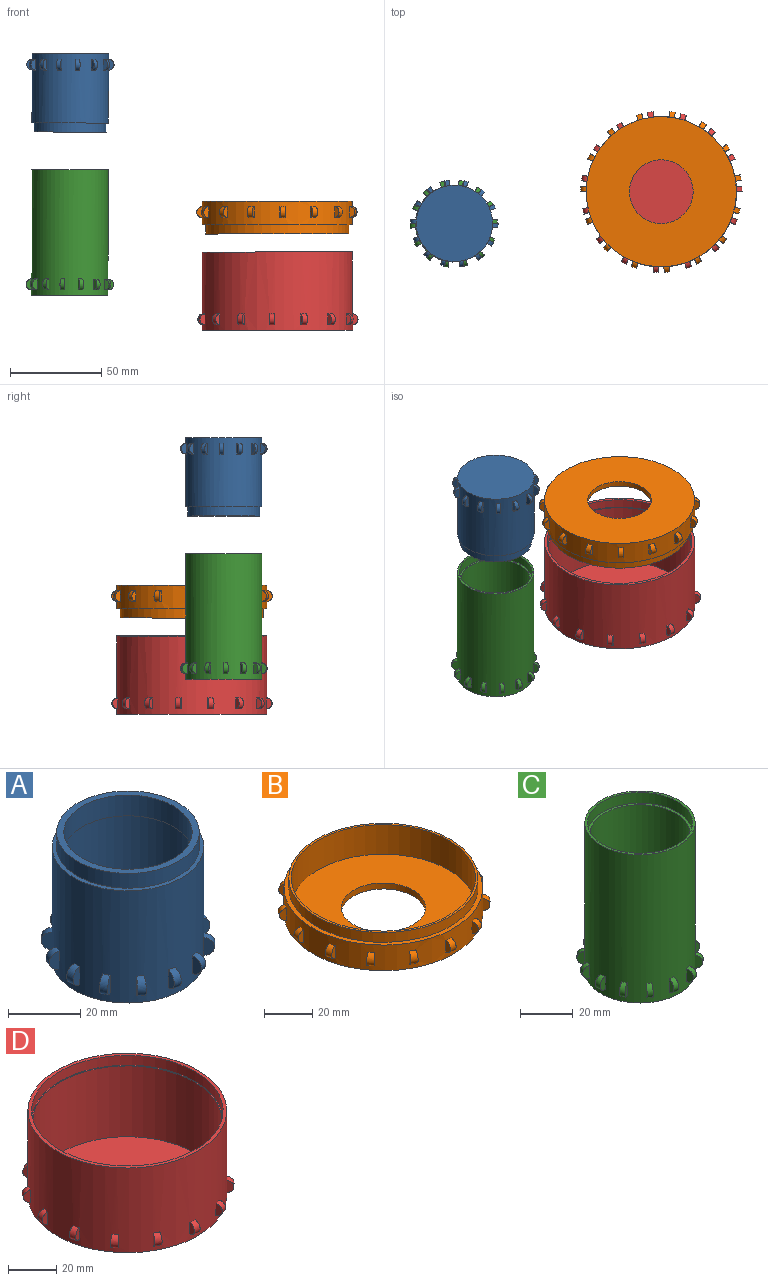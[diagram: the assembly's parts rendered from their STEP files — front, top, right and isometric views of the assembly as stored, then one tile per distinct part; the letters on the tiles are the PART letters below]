
ASSEMBLY  parts=4 mates=2
PART A: 51 faces, bbox 48.1x47.7x43 mm
  f0: torus R=21.01mm, axis (0,0,-1), area 21.6mm2, adj f22,f48,f49
  f1: torus R=21.01mm, axis (0,0,-1), area 21.6mm2, adj f22,f46,f47
  f2: torus R=21.01mm, axis (0,0,-1), area 21.6mm2, adj f22,f44,f45
  f3: torus R=21.01mm, axis (0,0,-1), area 21.6mm2, adj f22,f42,f43
  f4: torus R=21.01mm, axis (0,0,-1), area 21.6mm2, adj f22,f40,f41
  f5: torus R=21.01mm, axis (0,0,-1), area 21.6mm2, adj f22,f38,f39
  f6: torus R=21.01mm, axis (0,0,-1), area 21.6mm2, adj f22,f36,f37
  f7: torus R=21.01mm, axis (0,0,-1), area 21.6mm2, adj f22,f34,f35
  f8: torus R=21.01mm, axis (0,0,-1), area 21.6mm2, adj f22,f32,f33
  f9: torus R=21.01mm, axis (0,0,-1), area 21.6mm2, adj f22,f30,f31
  f10: torus R=21.01mm, axis (0,0,-1), area 21.6mm2, adj f22,f28,f29
  f11: torus R=21.01mm, axis (0,0,-1), area 21.6mm2, adj f22,f26,f27
  f12: torus R=21.01mm, axis (0,0,-1), area 21.6mm2, adj f22,f24,f25
  f13: torus R=21.01mm, axis (0,0,-1), area 21.6mm2, adj f22,f23,f50
  f14: cylinder r=19.75mm len=39.5mm, axis (0,0,-1), area 620.5mm2, adj f15,f16
  f15: plane 39.5x39.5mm, normal (0,0,1), area 235.6mm2, adj f14,f17
  f16: plane 42x42mm, normal (0,0,1), area 160mm2, adj f14,f22
  f17: cylinder r=17.75mm len=35.5mm, axis (0,0,-1), area 780.7mm2, adj f15,f19
  f18: cylinder r=19mm len=38mm, axis (0,0,-1), area 4058.9mm2, adj f19,f20
  f19: plane 38x38mm, normal (0,0,-1), area 144.3mm2, adj f17,f18
  f20: plane 38x38mm, normal (0,0,1), area 1134.1mm2, adj f18
  f21: plane 42x42mm, normal (0,0,-1), area 1385.4mm2, adj f22
  f22: cylinder r=21mm len=42mm, axis (0,0,-1), area 4838.1mm2, adj f0,f1,f2,f3,f4,f5,f6,f7
  f23: plane 6x2.83mm, normal (0.34,0.94,0), area 14.2mm2, adj f13,f22
  f24: plane 6x3.01mm, normal (0,-1,0), area 14.2mm2, adj f12,f22
  f25: plane 6x3mm, normal (-0.1,1,0), area 14.2mm2, adj f12,f22
  f26: plane 6x2.71mm, normal (0.43,-0.9,0), area 14.2mm2, adj f11,f22
  f27: plane 6x2.57mm, normal (-0.52,0.85,0), area 14.2mm2, adj f11,f22
  f28: plane 6x2.36mm, normal (0.78,-0.62,0), area 14.2mm2, adj f10,f22
  f29: plane 6x2.53mm, normal (-0.84,0.54,0), area 14.2mm2, adj f10,f22
  f30: plane 6x2.94mm, normal (0.97,-0.22,0), area 14.2mm2, adj f9,f22
  f31: plane 6x2.99mm, normal (-0.99,0.12,0), area 14.2mm2, adj f9,f22
  f32: plane 6x2.94mm, normal (0.97,0.22,0), area 14.2mm2, adj f8,f22
  f33: plane 6x2.86mm, normal (-0.95,-0.32,0), area 14.2mm2, adj f8,f22
  f34: plane 6x2.36mm, normal (0.78,0.62,0), area 14.2mm2, adj f7,f22
  f35: plane 6x2.16mm, normal (-0.72,-0.7,0), area 14.2mm2, adj f7,f22
  f36: plane 6x2.71mm, normal (0.43,0.9,0), area 14.2mm2, adj f6,f22
  f37: plane 6x2.83mm, normal (-0.34,-0.94,0), area 14.2mm2, adj f6,f22
  f38: plane 6x3.01mm, normal (0,1,0), area 14.2mm2, adj f5,f22
  f39: plane 6x3mm, normal (0.1,-1,0), area 14.2mm2, adj f5,f22
  f40: plane 6x2.71mm, normal (-0.43,0.9,0), area 14.2mm2, adj f4,f22
  f41: plane 6x2.57mm, normal (0.52,-0.85,0), area 14.2mm2, adj f4,f22
  f42: plane 6x2.36mm, normal (-0.78,0.62,0), area 14.2mm2, adj f3,f22
  f43: plane 6x2.53mm, normal (0.84,-0.54,0), area 14.2mm2, adj f3,f22
  f44: plane 6x2.94mm, normal (-0.97,0.22,0), area 14.2mm2, adj f2,f22
  f45: plane 6x2.99mm, normal (0.99,-0.12,0), area 14.2mm2, adj f2,f22
  f46: plane 6x2.94mm, normal (-0.97,-0.22,0), area 14.2mm2, adj f1,f22
  f47: plane 6x2.86mm, normal (0.95,0.32,0), area 14.2mm2, adj f1,f22
  f48: plane 6x2.36mm, normal (-0.78,-0.62,0), area 14.2mm2, adj f0,f22
  f49: plane 6x2.16mm, normal (0.72,0.7,0), area 14.2mm2, adj f0,f22
  f50: plane 6x2.71mm, normal (-0.43,-0.9,0), area 14.2mm2, adj f13,f22
PART B: 53 faces, bbox 88.1x88.3x18 mm
  f0: plane 78.5x78.5mm, normal (0,0,1), area 243.5mm2, adj f1,f3
  f1: cylinder r=38.25mm len=76.5mm, axis (0,0,-1), area 3605mm2, adj f0,f2
  f2: plane 76.5x76.5mm, normal (0,0,1), area 3634.2mm2, adj f1,f52
  f3: cylinder r=39.25mm len=78.5mm, axis (0,0,1), area 1233.1mm2, adj f0,f4
  f4: plane 82.5x82.5mm, normal (0,0,1), area 505.8mm2, adj f3,f51
  f5: plane 6x2.82mm, normal (0.34,0.94,0), area 14.1mm2, adj f7,f51
  f6: plane 6x2.74mm, normal (-0.41,-0.91,0), area 14.1mm2, adj f7,f51
  f7: torus R=41.25mm, axis (0,0,-1), area 28.4mm2, adj f5,f6,f51
  f8: plane 6x2.23mm, normal (-0.74,-0.67,0), area 14.1mm2, adj f9,f51
  f9: torus R=41.25mm, axis (0,0,-1), area 28.4mm2, adj f8,f10,f51
  f10: plane 6x2.16mm, normal (0.69,0.72,0), area 14.1mm2, adj f9,f51
  f11: plane 6x2.85mm, normal (-0.95,-0.31,0), area 14.1mm2, adj f12,f51
  f12: torus R=41.25mm, axis (0,0,-1), area 28.4mm2, adj f11,f13,f51
  f13: plane 6x2.78mm, normal (0.93,0.37,0), area 14.1mm2, adj f12,f51
  f14: plane 6x2.98mm, normal (-0.99,0.1,0), area 14.1mm2, adj f15,f51
  f15: torus R=41.25mm, axis (0,0,-1), area 28.4mm2, adj f14,f16,f51
  f16: plane 6x3mm, normal (1,-0.03,0), area 14.1mm2, adj f15,f51
  f17: plane 6x2.6mm, normal (-0.87,0.5,0), area 14.1mm2, adj f18,f51
  f18: torus R=41.25mm, axis (0,0,-1), area 28.4mm2, adj f17,f19,f51
  f19: plane 6x2.7mm, normal (0.9,-0.44,0), area 14.1mm2, adj f18,f51
  f20: plane 6x2.43mm, normal (-0.59,0.81,0), area 14.1mm2, adj f21,f51
  f21: torus R=41.25mm, axis (0,0,-1), area 28.4mm2, adj f20,f22,f51
  f22: plane 6x2.3mm, normal (0.64,-0.77,0), area 14.1mm2, adj f21,f51
  f23: plane 6x2.93mm, normal (-0.21,0.98,0), area 14.1mm2, adj f24,f51
  f24: torus R=41.25mm, axis (0,0,-1), area 28.4mm2, adj f23,f25,f51
  f25: plane 6x2.88mm, normal (0.28,-0.96,0), area 14.1mm2, adj f24,f51
  f26: plane 6x2.93mm, normal (0.21,0.98,0), area 14.1mm2, adj f27,f51
  f27: torus R=41.25mm, axis (0,0,-1), area 28.4mm2, adj f26,f28,f51
  f28: plane 6x2.97mm, normal (-0.14,-0.99,0), area 14.1mm2, adj f27,f51
  f29: plane 6x2.43mm, normal (0.59,0.81,0), area 14.1mm2, adj f30,f51
  f30: torus R=41.25mm, axis (0,0,-1), area 28.4mm2, adj f29,f31,f51
  f31: plane 6x2.54mm, normal (-0.53,-0.85,0), area 14.1mm2, adj f30,f51
  f32: plane 6x2.6mm, normal (0.87,0.5,0), area 14.1mm2, adj f33,f51
  f33: torus R=41.25mm, axis (0,0,-1), area 28.4mm2, adj f32,f34,f51
  f34: plane 6x2.49mm, normal (-0.83,-0.56,0), area 14.1mm2, adj f33,f51
  f35: plane 6x2.98mm, normal (0.99,0.1,0), area 14.1mm2, adj f36,f51
  f36: torus R=41.25mm, axis (0,0,-1), area 28.4mm2, adj f35,f37,f51
  f37: plane 6x2.95mm, normal (-0.98,-0.17,0), area 14.1mm2, adj f36,f51
  f38: plane 6x2.85mm, normal (0.95,-0.31,0), area 14.1mm2, adj f39,f51
  f39: torus R=41.25mm, axis (0,0,-1), area 28.4mm2, adj f38,f40,f51
  f40: plane 6x2.91mm, normal (-0.97,0.24,0), area 14.1mm2, adj f39,f51
  f41: plane 6x2.23mm, normal (0.74,-0.67,0), area 14.1mm2, adj f42,f51
  f42: torus R=41.25mm, axis (0,0,-1), area 28.4mm2, adj f41,f43,f51
  f43: plane 6x2.36mm, normal (-0.79,0.62,0), area 14.1mm2, adj f42,f51
  f44: plane 6x2.74mm, normal (0.41,-0.91,0), area 14.1mm2, adj f45,f51
  f45: torus R=41.25mm, axis (0,0,-1), area 28.4mm2, adj f44,f46,f51
  f46: plane 6x2.65mm, normal (-0.47,0.88,0), area 14.1mm2, adj f45,f51
  f47: plane 6x3mm, normal (0,-1,0), area 14.1mm2, adj f48,f51
  f48: torus R=41.25mm, axis (0,0,-1), area 28.4mm2, adj f47,f49,f51
  f49: plane 6x2.99mm, normal (-0.07,1,0), area 14.1mm2, adj f48,f51
  f50: plane 82.5x82.5mm, normal (0,0,-1), area 4383.5mm2, adj f51,f52
  f51: cylinder r=41.25mm len=82.5mm, axis (0,0,-1), area 3110.2mm2, adj f4,f5,f6,f7,f8,f9,f10,f11
  f52: cylinder r=17.5mm len=35mm, axis (0,0,-1), area 329.9mm2, adj f2,f50
PART C: 49 faces, bbox 48.1x47.7x69 mm
  f0: torus R=21mm, axis (0,0,-1), area 21.5mm2, adj f20,f46,f47
  f1: torus R=21mm, axis (0,0,-1), area 21.5mm2, adj f20,f44,f45
  f2: torus R=21mm, axis (0,0,-1), area 21.5mm2, adj f20,f42,f43
  f3: torus R=21mm, axis (0,0,-1), area 21.5mm2, adj f20,f40,f41
  f4: torus R=21mm, axis (0,0,-1), area 21.5mm2, adj f20,f38,f39
  f5: torus R=21mm, axis (0,0,-1), area 21.5mm2, adj f20,f36,f37
  f6: torus R=21mm, axis (0,0,-1), area 21.5mm2, adj f20,f34,f35
  f7: torus R=21mm, axis (0,0,-1), area 21.5mm2, adj f20,f32,f33
  f8: torus R=21mm, axis (0,0,-1), area 21.5mm2, adj f20,f30,f31
  f9: torus R=21mm, axis (0,0,-1), area 21.5mm2, adj f20,f28,f29
  f10: torus R=21mm, axis (0,0,-1), area 21.5mm2, adj f20,f26,f27
  f11: torus R=21mm, axis (0,0,-1), area 21.5mm2, adj f20,f24,f25
  f12: torus R=21mm, axis (0,0,-1), area 21.5mm2, adj f20,f22,f23
  f13: torus R=21mm, axis (0,0,-1), area 21.5mm2, adj f20,f21,f48
  f14: plane 40x40mm, normal (0,0,1), area 122.5mm2, adj f15,f17
  f15: cylinder r=19mm len=62mm, axis (0,0,-1), area 7401.6mm2, adj f14,f16
  f16: plane 38x38mm, normal (0,0,1), area 1134.1mm2, adj f15
  f17: cylinder r=20mm len=40mm, axis (0,0,-1), area 628.3mm2, adj f14,f18
  f18: plane 42x42mm, normal (0,0,1), area 128.8mm2, adj f17,f20
  f19: plane 42x42mm, normal (0,0,-1), area 1385.4mm2, adj f20
  f20: cylinder r=21mm len=69mm, axis (0,0,-1), area 8928.4mm2, adj f0,f1,f2,f3,f4,f5,f6,f7
  f21: plane 6x2.82mm, normal (0.34,0.94,0), area 14.1mm2, adj f13,f20
  f22: plane 6x3mm, normal (0,-1,0), area 14.1mm2, adj f12,f20
  f23: plane 6x2.99mm, normal (-0.1,1,0), area 14.1mm2, adj f12,f20
  f24: plane 6x2.7mm, normal (0.43,-0.9,0), area 14.1mm2, adj f11,f20
  f25: plane 6x2.56mm, normal (-0.52,0.85,0), area 14.1mm2, adj f11,f20
  f26: plane 6x2.35mm, normal (0.78,-0.62,0), area 14.1mm2, adj f10,f20
  f27: plane 6x2.52mm, normal (-0.84,0.54,0), area 14.1mm2, adj f10,f20
  f28: plane 6x2.92mm, normal (0.97,-0.22,0), area 14.1mm2, adj f9,f20
  f29: plane 6x2.98mm, normal (-0.99,0.12,0), area 14.1mm2, adj f9,f20
  f30: plane 6x2.92mm, normal (0.97,0.22,0), area 14.1mm2, adj f8,f20
  f31: plane 6x2.84mm, normal (-0.95,-0.32,0), area 14.1mm2, adj f8,f20
  f32: plane 6x2.35mm, normal (0.78,0.62,0), area 14.1mm2, adj f7,f20
  f33: plane 6x2.15mm, normal (-0.72,-0.7,0), area 14.1mm2, adj f7,f20
  f34: plane 6x2.7mm, normal (0.43,0.9,0), area 14.1mm2, adj f6,f20
  f35: plane 6x2.82mm, normal (-0.34,-0.94,0), area 14.1mm2, adj f6,f20
  f36: plane 6x3mm, normal (0,1,0), area 14.1mm2, adj f5,f20
  f37: plane 6x2.99mm, normal (0.1,-1,0), area 14.1mm2, adj f5,f20
  f38: plane 6x2.7mm, normal (-0.43,0.9,0), area 14.1mm2, adj f4,f20
  f39: plane 6x2.56mm, normal (0.52,-0.85,0), area 14.1mm2, adj f4,f20
  f40: plane 6x2.35mm, normal (-0.78,0.62,0), area 14.1mm2, adj f3,f20
  f41: plane 6x2.52mm, normal (0.84,-0.54,0), area 14.1mm2, adj f3,f20
  f42: plane 6x2.92mm, normal (-0.97,0.22,0), area 14.1mm2, adj f2,f20
  f43: plane 6x2.98mm, normal (0.99,-0.12,0), area 14.1mm2, adj f2,f20
  f44: plane 6x2.92mm, normal (-0.97,-0.22,0), area 14.1mm2, adj f1,f20
  f45: plane 6x2.84mm, normal (0.95,0.32,0), area 14.1mm2, adj f1,f20
  f46: plane 6x2.35mm, normal (-0.78,-0.62,0), area 14.1mm2, adj f0,f20
  f47: plane 6x2.15mm, normal (0.72,0.7,0), area 14.1mm2, adj f0,f20
  f48: plane 6x2.7mm, normal (-0.43,-0.9,0), area 14.1mm2, adj f13,f20
PART D: 52 faces, bbox 88.1x88.3x43 mm
  f0: torus R=41.25mm, axis (0,0,-1), area 28.4mm2, adj f17,f45,f46
  f1: torus R=41.25mm, axis (0,0,-1), area 28.4mm2, adj f17,f43,f44
  f2: torus R=41.25mm, axis (0,0,-1), area 28.4mm2, adj f17,f41,f42
  f3: torus R=41.25mm, axis (0,0,-1), area 28.4mm2, adj f17,f39,f40
  f4: torus R=41.25mm, axis (0,0,-1), area 28.4mm2, adj f17,f37,f38
  f5: torus R=41.25mm, axis (0,0,-1), area 28.4mm2, adj f17,f35,f36
  f6: torus R=41.25mm, axis (0,0,-1), area 28.4mm2, adj f17,f33,f34
  f7: torus R=41.25mm, axis (0,0,-1), area 28.4mm2, adj f17,f31,f32
  f8: torus R=41.25mm, axis (0,0,-1), area 28.4mm2, adj f17,f29,f30
  f9: torus R=41.25mm, axis (0,0,-1), area 28.4mm2, adj f17,f27,f28
  f10: torus R=41.25mm, axis (0,0,-1), area 28.4mm2, adj f17,f25,f26
  f11: torus R=41.25mm, axis (0,0,-1), area 28.4mm2, adj f17,f23,f24
  f12: torus R=41.25mm, axis (0,0,-1), area 28.4mm2, adj f17,f21,f22
  f13: torus R=41.25mm, axis (0,0,-1), area 28.4mm2, adj f17,f19,f20
  f14: torus R=41.25mm, axis (0,0,-1), area 28.4mm2, adj f17,f18,f47
  f15: plane 82.5x82.5mm, normal (0,0,1), area 381.7mm2, adj f17,f48
  f16: plane 82.5x82.5mm, normal (0,0,-1), area 5345.6mm2, adj f17
  f17: cylinder r=41.25mm len=82.5mm, axis (0,0,-1), area 10885.6mm2, adj f0,f1,f2,f3,f4,f5,f6,f7
  f18: plane 6x2.82mm, normal (0.34,0.94,0), area 14.1mm2, adj f14,f17
  f19: plane 6x3mm, normal (0,-1,0), area 14.1mm2, adj f13,f17
  f20: plane 6x2.99mm, normal (-0.07,1,0), area 14.1mm2, adj f13,f17
  f21: plane 6x2.74mm, normal (0.41,-0.91,0), area 14.1mm2, adj f12,f17
  f22: plane 6x2.65mm, normal (-0.47,0.88,0), area 14.1mm2, adj f12,f17
  f23: plane 6x2.23mm, normal (0.74,-0.67,0), area 14.1mm2, adj f11,f17
  f24: plane 6x2.36mm, normal (-0.79,0.62,0), area 14.1mm2, adj f11,f17
  f25: plane 6x2.85mm, normal (0.95,-0.31,0), area 14.1mm2, adj f10,f17
  f26: plane 6x2.91mm, normal (-0.97,0.24,0), area 14.1mm2, adj f10,f17
  f27: plane 6x2.98mm, normal (0.99,0.1,0), area 14.1mm2, adj f9,f17
  f28: plane 6x2.95mm, normal (-0.98,-0.17,0), area 14.1mm2, adj f9,f17
  f29: plane 6x2.6mm, normal (0.87,0.5,0), area 14.1mm2, adj f8,f17
  f30: plane 6x2.49mm, normal (-0.83,-0.56,0), area 14.1mm2, adj f8,f17
  f31: plane 6x2.43mm, normal (0.59,0.81,0), area 14.1mm2, adj f7,f17
  f32: plane 6x2.54mm, normal (-0.53,-0.85,0), area 14.1mm2, adj f7,f17
  f33: plane 6x2.93mm, normal (0.21,0.98,0), area 14.1mm2, adj f6,f17
  f34: plane 6x2.97mm, normal (-0.14,-0.99,0), area 14.1mm2, adj f6,f17
  f35: plane 6x2.93mm, normal (-0.21,0.98,0), area 14.1mm2, adj f5,f17
  f36: plane 6x2.88mm, normal (0.28,-0.96,0), area 14.1mm2, adj f5,f17
  f37: plane 6x2.43mm, normal (-0.59,0.81,0), area 14.1mm2, adj f4,f17
  f38: plane 6x2.3mm, normal (0.64,-0.77,0), area 14.1mm2, adj f4,f17
  f39: plane 6x2.6mm, normal (-0.87,0.5,0), area 14.1mm2, adj f3,f17
  f40: plane 6x2.7mm, normal (0.9,-0.44,0), area 14.1mm2, adj f3,f17
  f41: plane 6x2.98mm, normal (-0.99,0.1,0), area 14.1mm2, adj f2,f17
  f42: plane 6x3mm, normal (1,-0.03,0), area 14.1mm2, adj f2,f17
  f43: plane 6x2.85mm, normal (-0.95,-0.31,0), area 14.1mm2, adj f1,f17
  f44: plane 6x2.78mm, normal (0.93,0.37,0), area 14.1mm2, adj f1,f17
  f45: plane 6x2.23mm, normal (-0.74,-0.67,0), area 14.1mm2, adj f0,f17
  f46: plane 6x2.16mm, normal (0.69,0.72,0), area 14.1mm2, adj f0,f17
  f47: plane 6x2.74mm, normal (-0.41,-0.91,0), area 14.1mm2, adj f14,f17
  f48: cylinder r=39.75mm len=79.5mm, axis (0,0,1), area 1248.8mm2, adj f15,f49
  f49: plane 79.5x79.5mm, normal (0,0,1), area 124.1mm2, adj f48,f51
  f50: plane 78.5x78.5mm, normal (0,0,1), area 4839.8mm2, adj f51
  f51: cylinder r=39.25mm len=78.5mm, axis (0,0,-1), area 8878.1mm2, adj f49,f50
PLACE A rot(axis=(0,-1,0),179.8deg) t=(-125.64,-22.16,140.32)mm
PLACE B rot(axis=(0,1,0),179.9deg) t=(-12.01,-4.6,59.37)mm
PLACE C rot(axis=(0,1,0),0.2deg) t=(-126.06,-22.16,7.65)mm
PLACE D rot(axis=(0,-1,0),0.1deg) t=(-11.92,-4.6,-11.55)mm
MATE slider C.f0 <-> A.f0  axis (0,0,-1) through (-125.95,-22.16,42.15)mm
MATE slider D.f0 <-> B.f1  axis (0,0,1) through (-11.98,-4.6,31.45)mm
